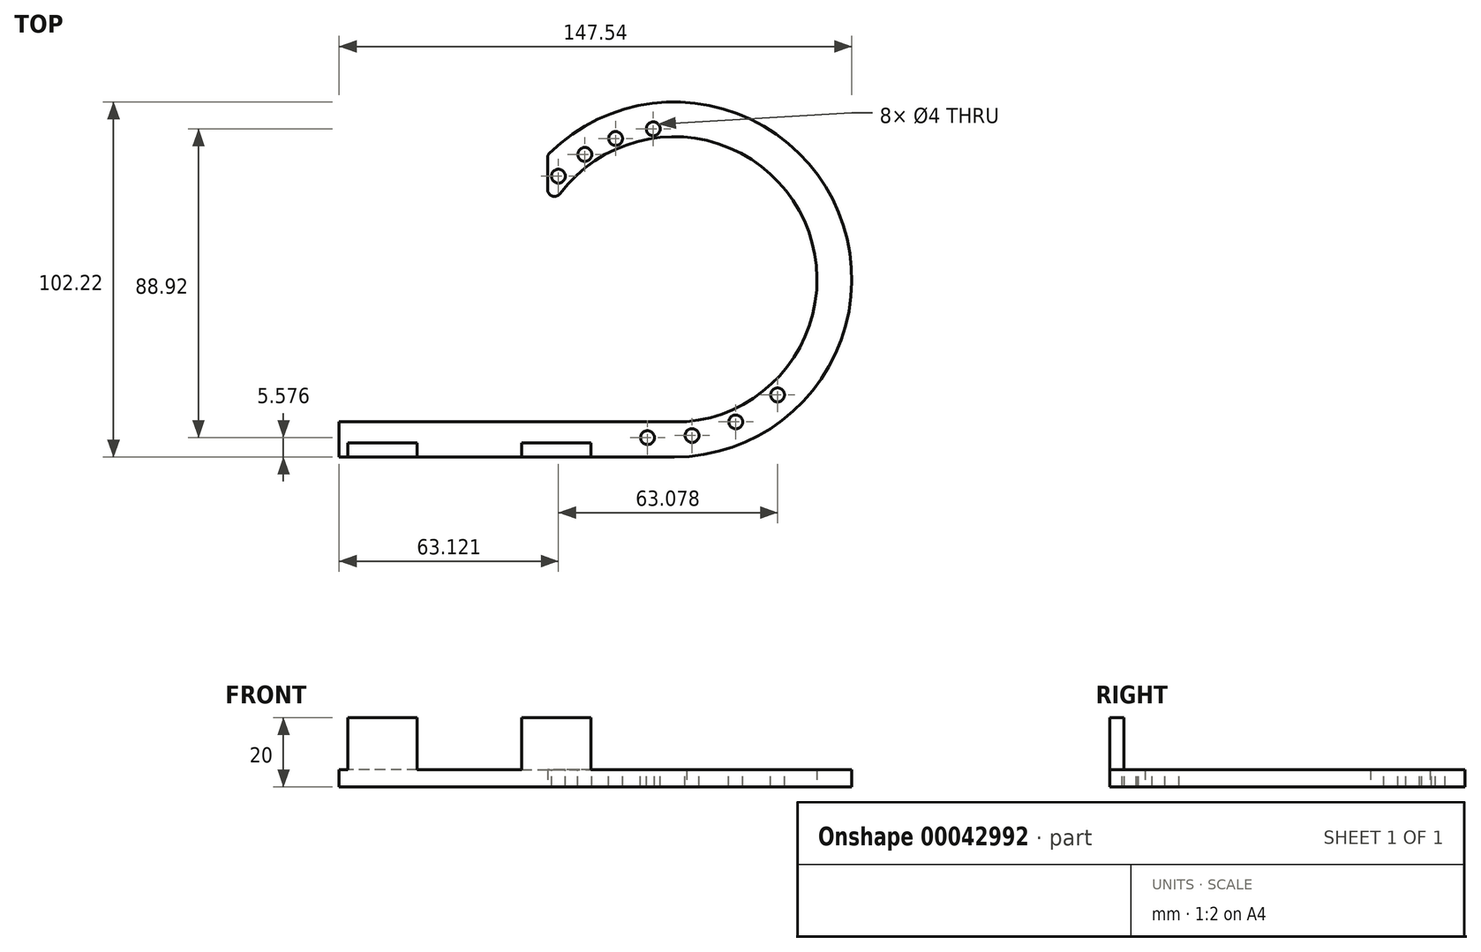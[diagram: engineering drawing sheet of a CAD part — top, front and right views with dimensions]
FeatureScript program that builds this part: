
annotation { "Feature Type Name" : "Feature", "Feature Type Description" : "" }
export const myFeature = defineFeature(function(context is Context, id is Id, definition is map)
    precondition{}
    {
        {
            var Q0;
            Q0=qCreatedBy(makeId("Top.planeOp"),FACE);
            var sketch = newSketch(context, id + "F0", { "sketchPlane" : qUnion([Q0])});
            skLineSegment(sketch, "E0.bottom", {"start": v(0, 10.15) * mm, "end": v(-100, 10.15) * mm});
            skLineSegment(sketch, "E0.top", {"start": v(-3.52, 0) * mm, "end": v(-100, 0) * mm});
            skLineSegment(sketch, "E0.right", {"start": v(-100, 10.15) * mm, "end": v(-100, 0) * mm});
            skArc(sketch, "E1", {"start": v(0, 10.15) * mm, "mid": v(30.64, 73.91) * mm, "end": v(-40, 70.15) * mm});
            skArc(sketch, "E2.0", {"start": v(-3.52, 0) * mm, "mid": v(43.56, 70.88) * mm, "end": v(-40, 86.96) * mm});
            skLineSegment(sketch, "E3", {"start": v(-40, 86.96) * mm, "end": v(-40, 70.15) * mm});
            skPoint(sketch, "E4", {"position": v(-100, 70.15) * mm});
            skSolve(sketch);
        }
        {
            var Q0;
            Q0 = qSketchRegion(id + "F0", true);
            extrude(context, id + "F1", {"entities" : qUnion([Q0]), "depth" : 5 * mm});
        }
        {
            var Q0;
            Q0=makeQuery(id+"F1.opExtrude","SWEPT_EDGE",EDGE,{"disambiguationData":[OSD([sQuery(id+"F0.wireOp",EDGE,"E1"),sQuery(id+"F0.wireOp",EDGE,"E3")])]});
            var Q1;
            Q1=makeQuery(id+"F1.opExtrude","SWEPT_EDGE",EDGE,{"disambiguationData":[OSD([sQuery(id+"F0.wireOp",EDGE,"E2.0"),sQuery(id+"F0.wireOp",EDGE,"E3")])]});
            fillet(context, id + "F2", {"entities" : qUnion([Q0, Q1]), "radius" : 2 * mm, "tangentPropagation" : true, "allowEdgeOverflow" : false});
        }
        {
            var Q0;
            Q0=makeQuery(id+"F1.opExtrude","CAP_FACE",FACE,{"disambiguationData":[OSD([sQuery(id+"F0.wireOp",EDGE,"E0.bottom"),sQuery(id+"F0.wireOp",EDGE,"E0.top"),sQuery(id+"F0.wireOp",EDGE,"E0.right"),sQuery(id+"F0.wireOp",EDGE,"E1"),sQuery(id+"F0.wireOp",EDGE,"E2.0"),sQuery(id+"F0.wireOp",EDGE,"E3")])],"isStart":false});
            var sketch = newSketch(context, id + "F3", { "sketchPlane" : qUnion([Q0])});
            skCircle(sketch, "E5", {"center": v(-36.88, 80.88) * mm, "radius": 2 * mm});
            skCircle(sketch, "E6", {"center": v(-20.41, 91.71) * mm, "radius": 2 * mm});
            skCircle(sketch, "E7", {"center": v(-9.58, 94.5) * mm, "radius": 2 * mm});
            skArc(sketch, "E8", {"start": v(-9.58, 94.5) * mm, "mid": v(-24.36, 89.96) * mm, "end": v(-36.88, 80.88) * mm, "construction": true});
            skCircle(sketch, "E9", {"center": v(-29.29, 87.12) * mm, "radius": 2 * mm});
            skCircle(sketch, "E10", {"center": v(-11.24, 5.58) * mm, "radius": 2 * mm});
            skCircle(sketch, "E11", {"center": v(14.16, 10.1) * mm, "radius": 2 * mm});
            skCircle(sketch, "E12", {"center": v(26.2, 17.89) * mm, "radius": 2 * mm});
            skCircle(sketch, "E13", {"center": v(1.57, 6.17) * mm, "radius": 2 * mm});
            skArc(sketch, "E14", {"start": v(-11.24, 5.58) * mm, "mid": v(8.72, 7.96) * mm, "end": v(26.2, 17.89) * mm, "construction": true});
            skSolve(sketch);
        }
        {
            var Q0;
            Q0 = qSketchRegion(id + "F3", true);
            extrude(context, id + "F4", {"entities" : qUnion([Q0]), "operationType" : NewBodyOperationType.REMOVE, "oppositeDirection" : true, "depth" : 5 * mm});
        }
        {
            var Q0;
            Q0=makeQuery(id+"F1.opExtrude","CAP_FACE",FACE,{"disambiguationData":[OSD([sQuery(id+"F0.wireOp",EDGE,"E0.bottom"),sQuery(id+"F0.wireOp",EDGE,"E0.top"),sQuery(id+"F0.wireOp",EDGE,"E0.right"),sQuery(id+"F0.wireOp",EDGE,"E1"),sQuery(id+"F0.wireOp",EDGE,"E2.0"),sQuery(id+"F0.wireOp",EDGE,"E3")])],"isStart":false});
            var sketch = newSketch(context, id + "F5", { "sketchPlane" : qUnion([Q0])});
            skLineSegment(sketch, "E15.right", {"start": v(-27.5, 4) * mm, "end": v(-27.5, 0) * mm});
            skLineSegment(sketch, "E16", {"start": v(-47.5, 4) * mm, "end": v(-47.5, 0) * mm});
            skLineSegment(sketch, "E17", {"start": v(-77.5, 4) * mm, "end": v(-77.5, 0) * mm});
            skLineSegment(sketch, "E18", {"start": v(-47.5, 4) * mm, "end": v(-27.5, 4) * mm});
            skLineSegment(sketch, "E19", {"start": v(-47.5, 0) * mm, "end": v(-27.5, 0) * mm});
            skLineSegment(sketch, "E20", {"start": v(-77.5, 4) * mm, "end": v(-97.5, 4) * mm});
            skLineSegment(sketch, "E21", {"start": v(-77.5, 0) * mm, "end": v(-97.5, 0) * mm});
            skLineSegment(sketch, "E22", {"start": v(-97.5, 4) * mm, "end": v(-97.5, 0) * mm});
            skSolve(sketch);
        }
        {
            var Q0;
            Q0 = qSketchRegion(id + "F5", true);
            extrude(context, id + "F6", {"entities" : qUnion([Q0]), "operationType" : NewBodyOperationType.ADD, "depth" : 15 * mm});
        }
    });
